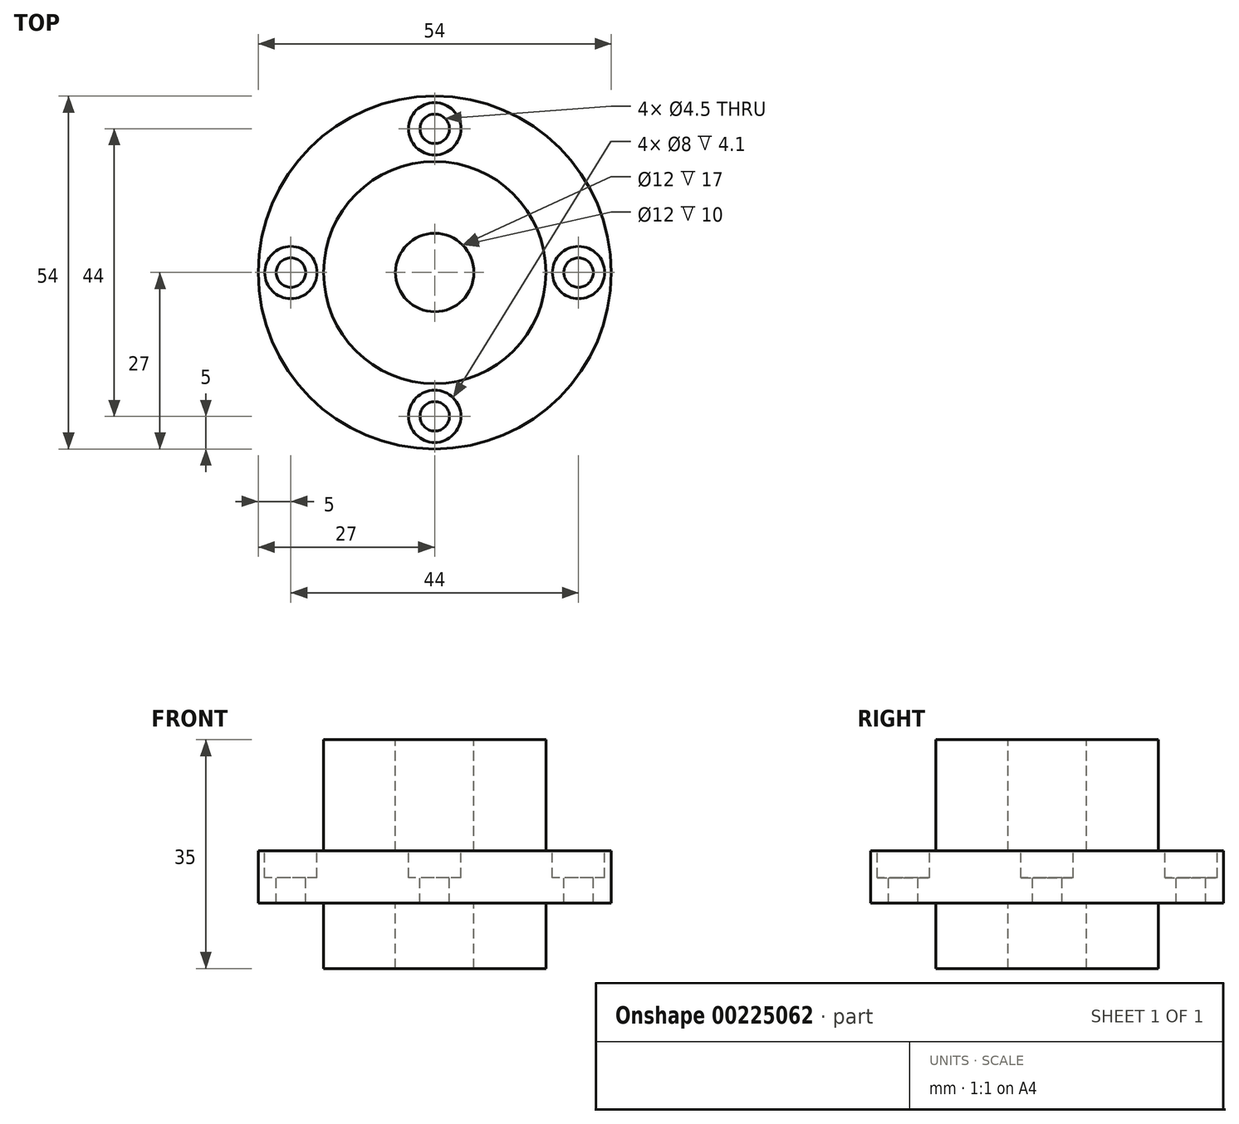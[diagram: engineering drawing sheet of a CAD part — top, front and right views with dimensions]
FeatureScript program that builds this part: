
annotation { "Feature Type Name" : "Feature", "Feature Type Description" : "" }
export const myFeature = defineFeature(function(context is Context, id is Id, definition is map)
    precondition{}
    {
        {
            var Q0;
            Q0=qCreatedBy(makeId("Top.planeOp"),FACE);
            var sketch = newSketch(context, id + "F0", { "sketchPlane" : qUnion([Q0])});
            skCircle(sketch, "E0", {"center": v(0, 0) * mm, "radius": 17 * mm});
            skCircle(sketch, "E1", {"center": v(0, 0) * mm, "radius": 6 * mm});
            skSolve(sketch);
        }
        {
            var Q0;
            Q0=qSketchRegion(id+"F0",true);
            extrude(context, id + "F1", {"entities" : qUnion([Q0]), "oppositeDirection" : true, "depth" : (35 - 18) * mm});
        }
        {
            var Q0;
            Q0=makeQuery(id+"F1.opExtrude","CAP_FACE",FACE,{"disambiguationData":[OSD([sQuery(id+"F0.wireOp",EDGE,"E0"),sQuery(id+"F0.wireOp",EDGE,"E1")])],"isStart":false});
            var sketch = newSketch(context, id + "F2", { "sketchPlane" : qUnion([Q0])});
            skCircle(sketch, "E2", {"center": v(0, 0) * mm, "radius": 27 * mm});
            skSolve(sketch);
        }
        {
            var Q0;
            Q0=qSketchRegion(id+"F2",true);
            extrude(context, id + "F3", {"entities" : qUnion([Q0]), "operationType" : NewBodyOperationType.ADD, "depth" : 8 * mm});
        }
        {
            var Q0;
            Q0=makeQuery(id+"F3.opExtrude","CAP_FACE",FACE,{"disambiguationData":[OSD([sQuery(id+"F2.wireOp",EDGE,"E2")])],"isStart":false});
            var sketch = newSketch(context, id + "F4", { "sketchPlane" : qUnion([Q0])});
            skCircle(sketch, "E3", {"center": v(0, 0) * mm, "radius": 6 * mm});
            skCircle(sketch, "E4", {"center": v(0, 0) * mm, "radius": 17 * mm});
            skSolve(sketch);
        }
        {
            var Q0;
            Q0=qSketchRegion(id+"F4",true);
            extrude(context, id + "F5", {"entities" : qUnion([Q0]), "operationType" : NewBodyOperationType.ADD, "depth" : 10 * mm});
        }
        {
            var Q0;
            {var subQ0=sQuery(id+"F2.wireOp",EDGE,"E2");Q0=makeQuery(id+"F3.boolean.opBoolean","SPLIT",FACE,{"disambiguationData":[TD([makeQuery(id+"F1.opExtrude","SWEPT_FACE",FACE,{"disambiguationData":[OSD([sQuery(id+"F0.wireOp",EDGE,"E0")])]})])],"derivedFrom":makeQuery(id+"F3.opExtrude","CAP_FACE",FACE,{"disambiguationData":[OSD([subQ0])],"isStart":true})});}
            var sketch = newSketch(context, id + "F6", { "sketchPlane" : qUnion([Q0])});
            skCircle(sketch, "E5", {"center": v(0, 0) * mm, "radius": 22 * mm});
            skPoint(sketch, "E6", {"position": v(-22, 0) * mm});
            skPoint(sketch, "E7", {"position": v(0, 22) * mm});
            skPoint(sketch, "E8", {"position": v(22, 0) * mm});
            skPoint(sketch, "E9", {"position": v(0, -22) * mm});
            skSolve(sketch);
        }
        {
            var Q0;
            Q0=sQuery(id+"F6.wireOp",VERTEX,"E7");
            var Q1;
            Q1=sQuery(id+"F6.wireOp",VERTEX,"E6");
            var Q2;
            Q2=sQuery(id+"F6.wireOp",VERTEX,"E9");
            var Q3;
            Q3=sQuery(id+"F6.wireOp",VERTEX,"E8");
            var Q4;
            Q4=makeQuery(id+"F1.opExtrude","SWEPT_BODY",BODY,{"disambiguationData":[OSD([sQuery(id+"F0.wireOp",EDGE,"E0"),sQuery(id+"F0.wireOp",EDGE,"E1")])]});
            hole(context, id + "F7", {"style" : HoleStyle.C_BORE, "endStyle" : HoleEndStyle.THROUGH, "holeDiameter" : 4.5 * mm, "cBoreDiameter" : 8 * mm, "cBoreDepth" : 4.1 * mm, "locations" : qUnion([Q0, Q1, Q2, Q3]), "scope" : qUnion([Q4]), "isTappedThrough" : true});
        }
    });
